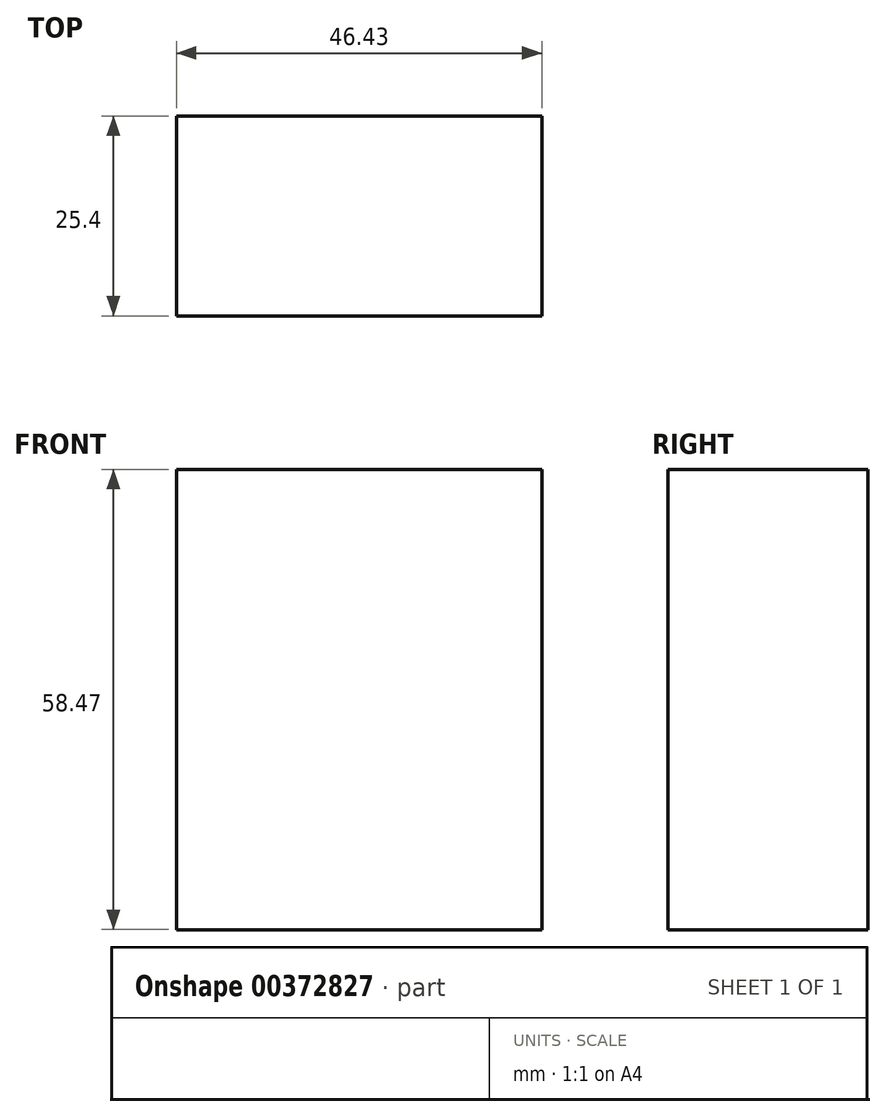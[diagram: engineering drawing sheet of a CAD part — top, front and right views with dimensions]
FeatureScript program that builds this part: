
annotation { "Feature Type Name" : "Feature", "Feature Type Description" : "" }
export const myFeature = defineFeature(function(context is Context, id is Id, definition is map)
    precondition{}
    {
        {
            var Q0;
            Q0=qCreatedBy(makeId("Front.planeOp"),FACE);
            var sketch = newSketch(context, id + "F0", { "sketchPlane" : qUnion([Q0])});
            skLineSegment(sketch, "E0.bottom", {"start": v(49.26, 22.77) * mm, "end": v(95.7, 22.77) * mm});
            skLineSegment(sketch, "E0.top", {"start": v(49.26, -35.7) * mm, "end": v(95.7, -35.7) * mm});
            skLineSegment(sketch, "E0.left", {"start": v(49.26, 22.77) * mm, "end": v(49.26, -35.7) * mm});
            skLineSegment(sketch, "E0.right", {"start": v(95.7, 22.77) * mm, "end": v(95.7, -35.7) * mm});
            skSolve(sketch);
        }
        {
            var Q0;
            Q0 = qSketchRegion(id + "F0", true);
            extrude(context, id + "F1", {"entities" : qUnion([Q0]), "depth" : 25.4 * mm});
        }
    });
